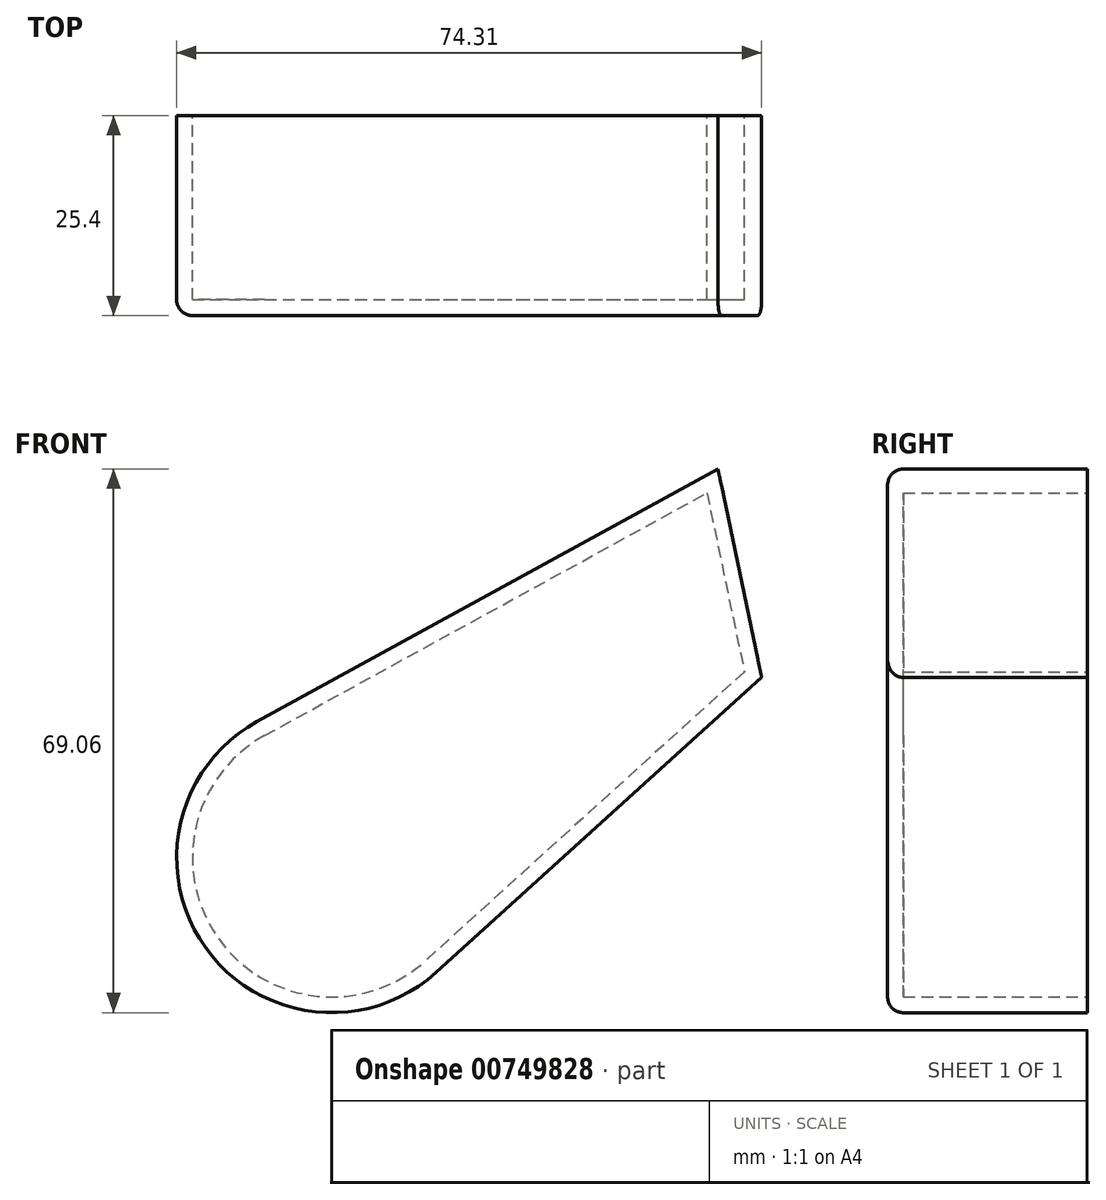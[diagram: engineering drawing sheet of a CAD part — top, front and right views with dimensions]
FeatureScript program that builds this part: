
annotation { "Feature Type Name" : "Feature", "Feature Type Description" : "" }
export const myFeature = defineFeature(function(context is Context, id is Id, definition is map)
    precondition{}
    {
        {
            var Q0;
            Q0=qCreatedBy(makeId("Front.planeOp"),FACE);
            var sketch = newSketch(context, id + "F0", { "sketchPlane" : qUnion([Q0])});
            skLineSegment(sketch, "E0", {"start": v(-110.03, 29.44) * mm, "end": v(-51.5, 61.53) * mm});
            skLineSegment(sketch, "E1", {"start": v(-51.5, 61.53) * mm, "end": v(-45.95, 35.06) * mm});
            skArc(sketch, "E2", {"start": v(-110.03, 29.44) * mm, "mid": v(-116.6, 0.74) * mm, "end": v(-87.33, -2.43) * mm});
            skLineSegment(sketch, "E3", {"start": v(-45.95, 35.06) * mm, "end": v(-87.33, -2.43) * mm});
            skSolve(sketch);
        }
        {
            var Q0;
            Q0=qSketchRegion(id+"F0",true);
            extrude(context, id + "F1", {"entities" : qUnion([Q0]), "depth" : 25.4 * mm, "offsetDistance" : 25.4 * mm});
        }
        {
            var Q0;
            Q0=makeQuery(id+"F1.opExtrude","CAP_EDGE",EDGE,{"disambiguationData":[OSD([sQuery(id+"F0.wireOp",EDGE,"E0")])],"isStart":false});
            fillet(context, id + "F2", {"entities" : qUnion([Q0]), "radius" : 2 * mm, "tangentPropagation" : true, "allowEdgeOverflow" : false});
        }
        {
            var Q0;
            Q0=makeQuery(id+"F1.opExtrude","CAP_FACE",FACE,{"disambiguationData":[OSD([sQuery(id+"F0.wireOp",EDGE,"E0"),sQuery(id+"F0.wireOp",EDGE,"E1"),sQuery(id+"F0.wireOp",EDGE,"E2"),sQuery(id+"F0.wireOp",EDGE,"E3")])],"isStart":true});
            shell(context, id + "F3", {"entities" : qUnion([Q0]), "thickness" : 2 * mm});
        }
    });
